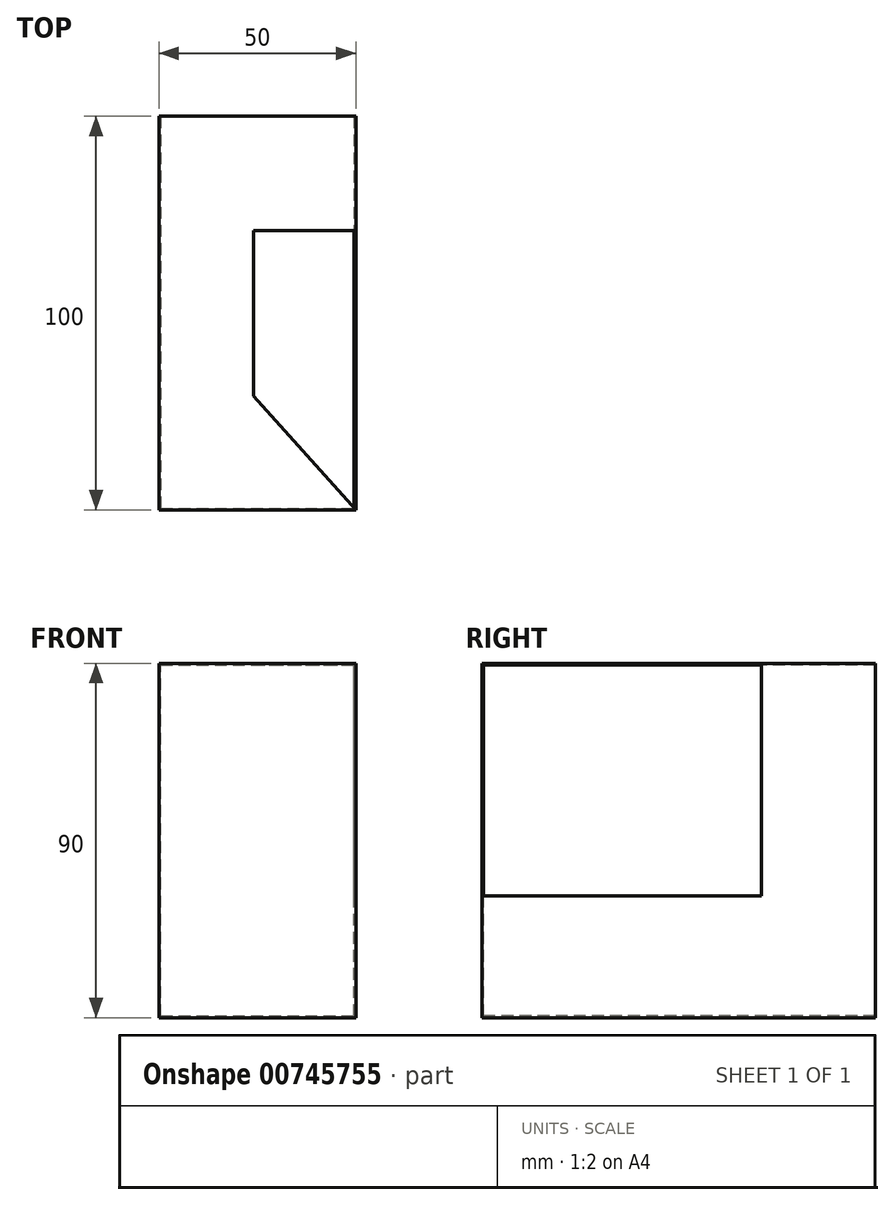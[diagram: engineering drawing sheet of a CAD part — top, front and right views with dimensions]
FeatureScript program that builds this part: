
annotation { "Feature Type Name" : "Feature", "Feature Type Description" : "" }
export const myFeature = defineFeature(function(context is Context, id is Id, definition is map)
    precondition{}
    {
        {
            var Q0;
            Q0=qCreatedBy(makeId("Front.planeOp"),FACE);
            var sketch = newSketch(context, id + "F0", { "sketchPlane" : qUnion([Q0])});
            skLineSegment(sketch, "E0.bottom", {"start": v(0, 0) * mm, "end": v(50, 0) * mm});
            skLineSegment(sketch, "E0.top", {"start": v(0, 90) * mm, "end": v(50, 90) * mm});
            skLineSegment(sketch, "E0.left", {"start": v(0, 0) * mm, "end": v(0, 90) * mm});
            skLineSegment(sketch, "E0.right", {"start": v(50, 0) * mm, "end": v(50, 90) * mm});
            skSolve(sketch);
        }
        {
            var Q0;
            Q0 = qSketchRegion(id + "F0", true);
            extrude(context, id + "F1", {"entities" : qUnion([Q0]), "oppositeDirection" : true, "depth" : 100 * mm, "offsetDistance" : 25 * mm});
        }
        {
            var Q0;
            Q0=makeQuery(id+"F1.opExtrude","CAP_FACE",FACE,{"disambiguationData":[OSD([sQuery(id+"F0.wireOp",EDGE,"E0.bottom"),sQuery(id+"F0.wireOp",EDGE,"E0.top"),sQuery(id+"F0.wireOp",EDGE,"E0.left"),sQuery(id+"F0.wireOp",EDGE,"E0.right")])],"isStart":false});
            shell(context, id + "F2", {"entities" : qUnion([Q0]), "thickness" : 0.4 * mm});
        }
        {
            var Q0;
            Q0=makeQuery(id+"F1.opExtrude","SWEPT_FACE",FACE,{"disambiguationData":[OSD([sQuery(id+"F0.wireOp",EDGE,"E0.top")])]});
            var sketch = newSketch(context, id + "F3", { "sketchPlane" : qUnion([Q0])});
            skLineSegment(sketch, "E1", {"start": v(50, 0) * mm, "end": v(24, 29) * mm});
            skLineSegment(sketch, "E2", {"start": v(24, 29) * mm, "end": v(24, 71) * mm});
            skLineSegment(sketch, "E3", {"start": v(24, 71) * mm, "end": v(50, 71) * mm});
            skLineSegment(sketch, "E4", {"start": v(50, 71) * mm, "end": v(50, 0) * mm});
            skSolve(sketch);
        }
        {
            var Q0;
            Q0 = qSketchRegion(id + "F3", true);
            extrude(context, id + "F4", {"entities" : qUnion([Q0]), "operationType" : NewBodyOperationType.REMOVE, "oppositeDirection" : true, "depth" : 59 * mm, "offsetDistance" : 25 * mm});
        }
    });
